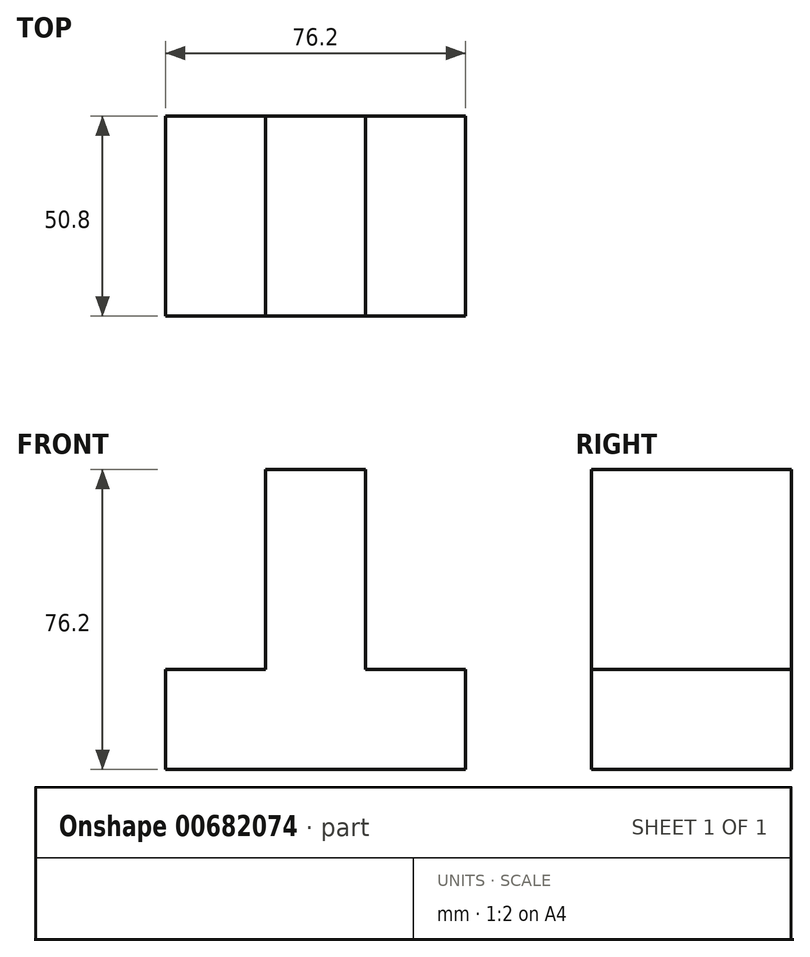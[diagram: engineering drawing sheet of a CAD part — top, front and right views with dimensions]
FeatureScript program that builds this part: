
annotation { "Feature Type Name" : "Feature", "Feature Type Description" : "" }
export const myFeature = defineFeature(function(context is Context, id is Id, definition is map)
    precondition{}
    {
        {
            var Q0;
            Q0=qCreatedBy(makeId("Front.planeOp"),FACE);
            var sketch = newSketch(context, id + "F0", { "sketchPlane" : qUnion([Q0])});
            skLineSegment(sketch, "E0", {"start": v(-50.8, 0) * mm, "end": v(25.4, 0) * mm});
            skLineSegment(sketch, "E1", {"start": v(-50.8, 0) * mm, "end": v(-50.8, 25.4) * mm});
            skLineSegment(sketch, "E2", {"start": v(-50.8, 25.4) * mm, "end": v(-25.4, 25.4) * mm});
            skLineSegment(sketch, "E3", {"start": v(-25.4, 25.4) * mm, "end": v(-25.4, 76.2) * mm});
            skLineSegment(sketch, "E4", {"start": v(-25.4, 76.2) * mm, "end": v(0, 76.2) * mm});
            skLineSegment(sketch, "E5", {"start": v(0, 76.2) * mm, "end": v(0, 25.4) * mm});
            skLineSegment(sketch, "E6", {"start": v(0, 25.4) * mm, "end": v(25.4, 25.4) * mm});
            skLineSegment(sketch, "E7", {"start": v(25.4, 25.4) * mm, "end": v(25.4, 0) * mm});
            skSolve(sketch);
        }
        {
            var Q0;
            Q0 = qSketchRegion(id + "F0", true);
            extrude(context, id + "F1", {"entities" : qUnion([Q0]), "depth" : 50.8 * mm, "offsetDistance" : 25.4 * mm});
        }
    });
